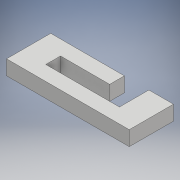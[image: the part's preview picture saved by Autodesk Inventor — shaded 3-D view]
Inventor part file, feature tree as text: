
AUTODESK INVENTOR PART (.ipt)
format: ipt  version: 2018 (Build 220112000, 112)  size: 105,984 bytes
history: native  units: mm
features: other x1, extrude x1, sketch x1
ambient origin geometry x8: Origin, YZ Plane, XZ Plane, XY Plane, X Axis, Y Axis, Z Axis, Center Point
bodies: Body1 (feature_tree)
feature tree (3):
  other  "Bryła1"
  extrude  "Wyciągnięcie proste1"  Depth=18.0mm
  sketch  "Szkic1"
